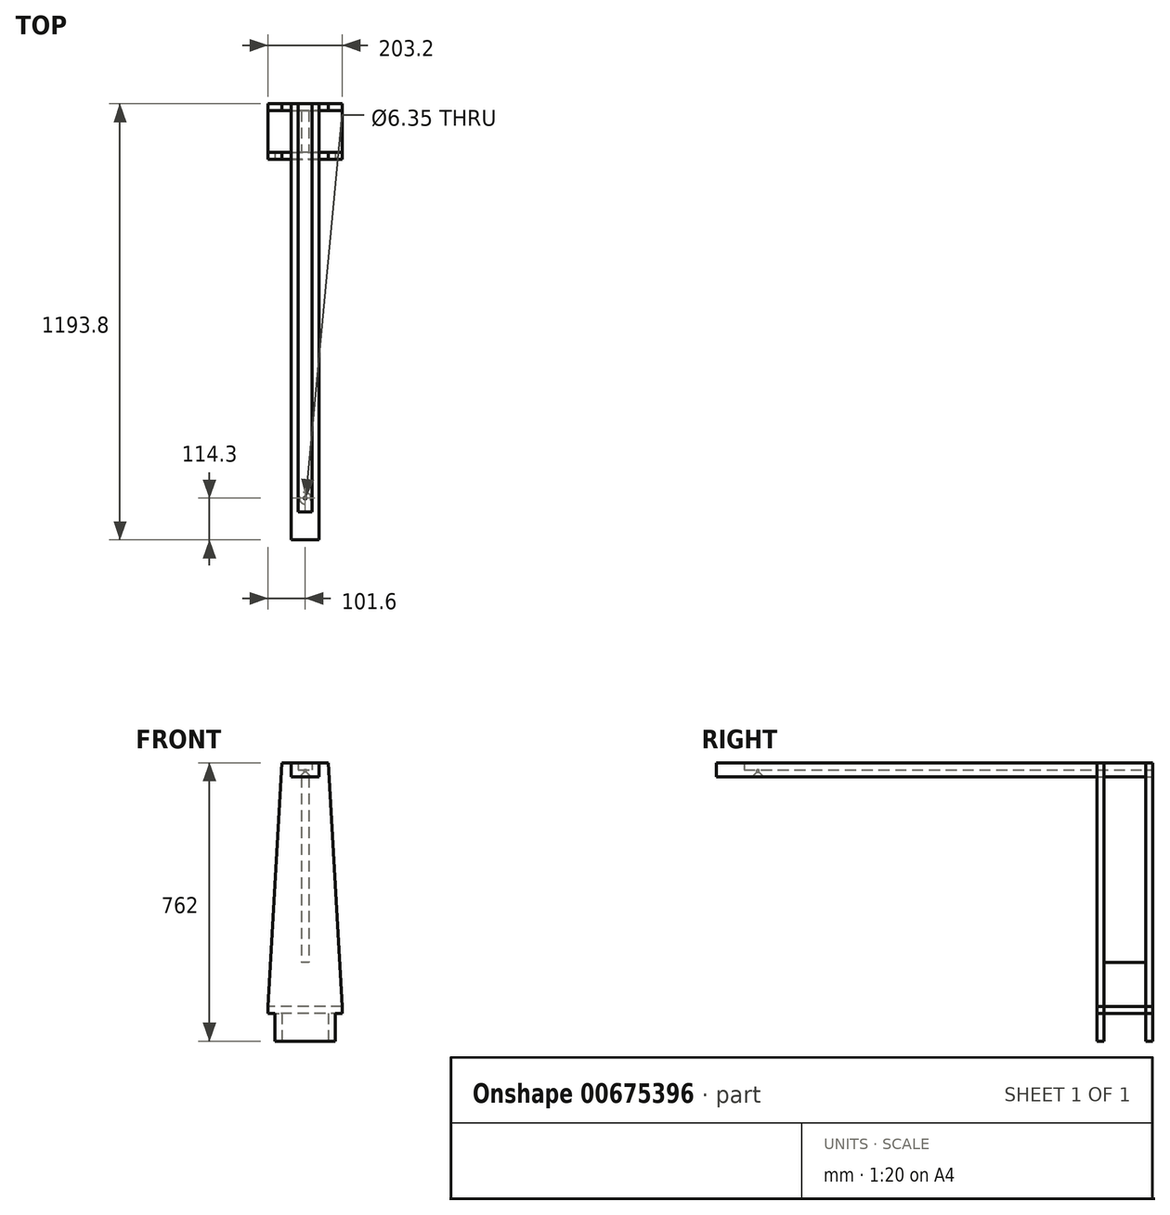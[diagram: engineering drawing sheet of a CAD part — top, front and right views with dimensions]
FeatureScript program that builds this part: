
annotation { "Feature Type Name" : "Feature", "Feature Type Description" : "" }
export const myFeature = defineFeature(function(context is Context, id is Id, definition is map)
    precondition{}
    {
        {
            var Q0;
            Q0=qCreatedBy(makeId("Top.planeOp"),FACE);
            var sketch = newSketch(context, id + "F0", { "sketchPlane" : qUnion([Q0])});
            skLineSegment(sketch, "E0.bottom", {"start": v(-101.6, -76.2) * mm, "end": v(101.6, -76.2) * mm});
            skLineSegment(sketch, "E0.top", {"start": v(-101.6, -57.15) * mm, "end": v(101.6, -57.15) * mm});
            skLineSegment(sketch, "E0.left", {"start": v(-101.6, -76.2) * mm, "end": v(-101.6, -57.15) * mm});
            skLineSegment(sketch, "E0.right", {"start": v(101.6, -76.2) * mm, "end": v(101.6, -57.15) * mm});
            skLineSegment(sketch, "E1.bottom", {"start": v(-101.6, 57.15) * mm, "end": v(101.6, 57.15) * mm});
            skLineSegment(sketch, "E1.top", {"start": v(-101.6, 76.2) * mm, "end": v(101.6, 76.2) * mm});
            skLineSegment(sketch, "E1.left", {"start": v(-101.6, 57.15) * mm, "end": v(-101.6, 76.2) * mm});
            skLineSegment(sketch, "E1.right", {"start": v(101.6, 57.15) * mm, "end": v(101.6, 76.2) * mm});
            skSolve(sketch);
        }
        {
            var Q0;
            Q0 = qSketchRegion(id + "F0", true);
            extrude(context, id + "F1", {"entities" : qUnion([Q0]), "depth" : 762 * mm, "offsetDistance" : 25.4 * mm});
        }
        {
            var Q0;
            Q0=makeQuery(id+"F1.opExtrude","SWEPT_FACE",FACE,{"disambiguationData":[OSD([sQuery(id+"F0.wireOp",EDGE,"E0.bottom")])]});
            var sketch = newSketch(context, id + "F2", { "sketchPlane" : qUnion([Q0])});
            skLineSegment(sketch, "E2", {"start": v(101.6, 762) * mm, "end": v(63.5, 762) * mm});
            skLineSegment(sketch, "E3", {"start": v(63.5, 762) * mm, "end": v(101.6, 95.25) * mm});
            skLineSegment(sketch, "E4", {"start": v(101.6, 95.25) * mm, "end": v(101.6, 762) * mm});
            skLineSegment(sketch, "E5", {"start": v(-63.5, 762) * mm, "end": v(-101.6, 762) * mm});
            skLineSegment(sketch, "E6", {"start": v(-101.6, 762) * mm, "end": v(-101.6, 95.25) * mm});
            skLineSegment(sketch, "E7", {"start": v(-101.6, 0) * mm, "end": v(-101.6, 76.2) * mm});
            skLineSegment(sketch, "E8", {"start": v(-101.6, 76.2) * mm, "end": v(-82.55, 76.2) * mm});
            skLineSegment(sketch, "E9", {"start": v(-82.55, 76.2) * mm, "end": v(-82.55, 0) * mm});
            skLineSegment(sketch, "E10", {"start": v(-101.6, 0) * mm, "end": v(-82.55, 0) * mm});
            skLineSegment(sketch, "E11", {"start": v(82.55, 76.2) * mm, "end": v(82.55, 0) * mm});
            skLineSegment(sketch, "E12", {"start": v(101.6, 0) * mm, "end": v(82.55, 0) * mm});
            skLineSegment(sketch, "E13", {"start": v(82.55, 76.2) * mm, "end": v(101.6, 76.2) * mm});
            skLineSegment(sketch, "E14", {"start": v(-63.5, 762) * mm, "end": v(-101.6, 95.25) * mm});
            skLineSegment(sketch, "E15", {"start": v(-38.1, 762) * mm, "end": v(38.1, 762) * mm});
            skLineSegment(sketch, "E16", {"start": v(38.1, 762) * mm, "end": v(38.1, 723.9) * mm});
            skLineSegment(sketch, "E17", {"start": v(38.1, 723.9) * mm, "end": v(-38.1, 723.9) * mm});
            skLineSegment(sketch, "E18", {"start": v(-38.1, 723.9) * mm, "end": v(-38.1, 762) * mm});
            skSolve(sketch);
        }
        {
            var Q0;
            Q0 = qSketchRegion(id + "F2", true);
            var Q1;
            Q1=makeQuery(id+"F2.imprint","IMPRINT",FACE,{"disambiguationData":[TD([[makeQuery(id+"F2.imprint","IMPRINT",EDGE,{"derivedFrom":sQuery(id+"F2.wireOp",EDGE,"E11")}),1.0]])]});
            extrude(context, id + "F3", {"entities" : qUnion([Q0, Q1]), "operationType" : NewBodyOperationType.REMOVE, "oppositeDirection" : true, "depth" : 25.4 * mm, "offsetDistance" : 25.4 * mm});
        }
        {
            var Q0;
            Q0=makeQuery(id+"F1.opExtrude","SWEPT_FACE",FACE,{"disambiguationData":[OSD([sQuery(id+"F0.wireOp",EDGE,"E1.bottom")])]});
            var sketch = newSketch(context, id + "F4", { "sketchPlane" : qUnion([Q0])});
            skLineSegment(sketch, "E19", {"start": v(-38.1, 762) * mm, "end": v(-38.1, 723.9) * mm});
            skLineSegment(sketch, "E20", {"start": v(-38.1, 723.9) * mm, "end": v(38.1, 723.9) * mm});
            skLineSegment(sketch, "E21", {"start": v(38.1, 723.9) * mm, "end": v(38.1, 762) * mm});
            skLineSegment(sketch, "E22", {"start": v(38.1, 762) * mm, "end": v(-38.1, 762) * mm});
            skLineSegment(sketch, "E23", {"start": v(101.6, 762) * mm, "end": v(63.5, 762) * mm});
            skLineSegment(sketch, "E24", {"start": v(-101.6, 762) * mm, "end": v(-101.6, 95.25) * mm});
            skLineSegment(sketch, "E25", {"start": v(-101.6, 95.25) * mm, "end": v(-63.5, 762) * mm});
            skLineSegment(sketch, "E26", {"start": v(-101.6, 762) * mm, "end": v(-63.5, 762) * mm});
            skLineSegment(sketch, "E27", {"start": v(101.6, 0) * mm, "end": v(101.6, 76.2) * mm});
            skLineSegment(sketch, "E28", {"start": v(101.6, 76.2) * mm, "end": v(63.5, 76.2) * mm});
            skLineSegment(sketch, "E29", {"start": v(63.5, 76.2) * mm, "end": v(63.5, 0) * mm});
            skLineSegment(sketch, "E30", {"start": v(63.5, 0) * mm, "end": v(101.6, 0) * mm});
            skLineSegment(sketch, "E31", {"start": v(-101.6, 0) * mm, "end": v(-101.6, 76.2) * mm});
            skLineSegment(sketch, "E32", {"start": v(-101.6, 76.2) * mm, "end": v(-63.5, 76.2) * mm});
            skLineSegment(sketch, "E33", {"start": v(-63.5, 76.2) * mm, "end": v(-63.5, 0) * mm});
            skLineSegment(sketch, "E34", {"start": v(-63.5, 0) * mm, "end": v(-101.6, 0) * mm});
            skLineSegment(sketch, "E35", {"start": v(63.5, 762) * mm, "end": v(101.6, 95.25) * mm});
            skLineSegment(sketch, "E36", {"start": v(101.6, 95.25) * mm, "end": v(101.6, 762) * mm});
            skSolve(sketch);
        }
        {
            var Q0;
            Q0 = qSketchRegion(id + "F4", true);
            extrude(context, id + "F5", {"entities" : qUnion([Q0]), "operationType" : NewBodyOperationType.REMOVE, "oppositeDirection" : true, "depth" : 25.4 * mm, "offsetDistance" : 25.4 * mm});
        }
        {
            var Q0;
            Q0=qCreatedBy(makeId("Front.planeOp"),FACE);
            var sketch = newSketch(context, id + "F6", { "sketchPlane" : qUnion([Q0])});
            skLineSegment(sketch, "E37", {"start": v(-38.1, 762) * mm, "end": v(-38.1, 723.9) * mm});
            skLineSegment(sketch, "E38", {"start": v(-38.1, 723.9) * mm, "end": v(38.1, 723.9) * mm});
            skLineSegment(sketch, "E39", {"start": v(38.1, 723.9) * mm, "end": v(38.1, 762) * mm});
            skLineSegment(sketch, "E40", {"start": v(38.1, 762) * mm, "end": v(19.05, 762) * mm});
            skLineSegment(sketch, "E41", {"start": v(19.05, 762) * mm, "end": v(19.05, 742.95) * mm});
            skLineSegment(sketch, "E42", {"start": v(19.05, 742.95) * mm, "end": v(-19.05, 742.95) * mm});
            skLineSegment(sketch, "E43", {"start": v(-19.05, 742.95) * mm, "end": v(-19.05, 762) * mm});
            skLineSegment(sketch, "E44", {"start": v(-19.05, 762) * mm, "end": v(-38.1, 762) * mm});
            skSolve(sketch);
        }
        {
            var Q0;
            Q0 = qSketchRegion(id + "F6", true);
            extrude(context, id + "F7", {"entities" : qUnion([Q0]), "depth" : 1117.6 * mm, "offsetDistance" : 25.4 * mm, "hasSecondDirection" : true, "secondDirectionOppositeDirection" : true, "secondDirectionDepth" : 76.2 * mm});
        }
        {
            var Q0;
            Q0=makeQuery(id+"F7.opExtrude","SWEPT_FACE",FACE,{"disambiguationData":[OSD([sQuery(id+"F6.wireOp",EDGE,"E42")])]});
            var sketch = newSketch(context, id + "F8", { "sketchPlane" : qUnion([Q0])});
            skCircle(sketch, "E45", {"center": v(0, -1003.3) * mm, "radius": 3.18 * mm});
            skSolve(sketch);
        }
        {
            var Q0;
            Q0 = qSketchRegion(id + "F8", true);
            extrude(context, id + "F9", {"entities" : qUnion([Q0]), "operationType" : NewBodyOperationType.REMOVE, "oppositeDirection" : true, "depth" : 25.4 * mm, "offsetDistance" : 25.4 * mm});
        }
        {
            var Q0;
            Q0=makeQuery(id+"F9.boolean.opBoolean","INTERSECT",EDGE,{"derivedFrom":[makeQuery(id+"F7.opExtrude","SWEPT_FACE",FACE,{"disambiguationData":[OSD([sQuery(id+"F6.wireOp",EDGE,"E38")])]}),makeQuery(id+"F9.opExtrude","SWEPT_FACE",FACE,{"disambiguationData":[OSD([sQuery(id+"F8.wireOp",EDGE,"E45")])]})]});
            chamfer(context, id + "F10", {"entities" : qUnion([Q0]), "width" : 12.7 * mm, "tangentPropagation" : true});
        }
        {
            var Q0;
            Q0=qCreatedBy(makeId("Front.planeOp"),FACE);
            var sketch = newSketch(context, id + "F11", { "sketchPlane" : qUnion([Q0])});
            skLineSegment(sketch, "E46.bottom", {"start": v(-19.05, 762) * mm, "end": v(19.05, 762) * mm});
            skLineSegment(sketch, "E46.top", {"start": v(-19.05, 742.95) * mm, "end": v(19.05, 742.95) * mm});
            skLineSegment(sketch, "E46.left", {"start": v(-19.05, 762) * mm, "end": v(-19.05, 742.95) * mm});
            skLineSegment(sketch, "E46.right", {"start": v(19.05, 762) * mm, "end": v(19.05, 742.95) * mm});
            skSolve(sketch);
        }
        {
            var Q0;
            Q0 = qSketchRegion(id + "F11", true);
            extrude(context, id + "F12", {"entities" : qUnion([Q0]), "operationType" : NewBodyOperationType.ADD, "depth" : 1117.6 * mm, "offsetDistance" : 25.4 * mm, "hasSecondDirection" : true, "secondDirectionOppositeDirection" : true, "secondDirectionDepth" : -1041.4 * mm});
        }
        {
            var Q0;
            Q0=qCreatedBy(makeId("Right.planeOp"),FACE);
            var sketch = newSketch(context, id + "F13", { "sketchPlane" : qUnion([Q0])});
            skLineSegment(sketch, "E47.bottom", {"start": v(57.15, 723.9) * mm, "end": v(-57.15, 723.9) * mm});
            skLineSegment(sketch, "E47.top", {"start": v(57.15, 215.9) * mm, "end": v(-57.15, 215.9) * mm});
            skLineSegment(sketch, "E47.left", {"start": v(57.15, 723.9) * mm, "end": v(57.15, 215.9) * mm});
            skLineSegment(sketch, "E47.right", {"start": v(-57.15, 723.9) * mm, "end": v(-57.15, 215.9) * mm});
            skSolve(sketch);
        }
        {
            var Q0;
            Q0 = qSketchRegion(id + "F13", true);
            extrude(context, id + "F14", {"entities" : qUnion([Q0]), "depth" : 9.52 * mm, "offsetDistance" : 25.4 * mm, "hasSecondDirection" : true, "secondDirectionOppositeDirection" : true, "secondDirectionDepth" : 9.52 * mm});
        }
        {
            var Q0;
            Q0=qCreatedBy(makeId("Right.planeOp"),FACE);
            var sketch = newSketch(context, id + "F15", { "sketchPlane" : qUnion([Q0])});
            skLineSegment(sketch, "E48.bottom", {"start": v(-57.15, 76.2) * mm, "end": v(57.15, 76.2) * mm});
            skLineSegment(sketch, "E48.top", {"start": v(-57.15, 95.25) * mm, "end": v(57.15, 95.25) * mm});
            skLineSegment(sketch, "E48.left", {"start": v(-57.15, 76.2) * mm, "end": v(-57.15, 95.25) * mm});
            skLineSegment(sketch, "E48.right", {"start": v(57.15, 76.2) * mm, "end": v(57.15, 95.25) * mm});
            skSolve(sketch);
        }
        {
            var Q0;
            Q0 = qSketchRegion(id + "F15", true);
            extrude(context, id + "F16", {"entities" : qUnion([Q0]), "depth" : 101.6 * mm, "offsetDistance" : 25.4 * mm, "hasSecondDirection" : true, "secondDirectionOppositeDirection" : true, "secondDirectionDepth" : 101.6 * mm});
        }
    });
